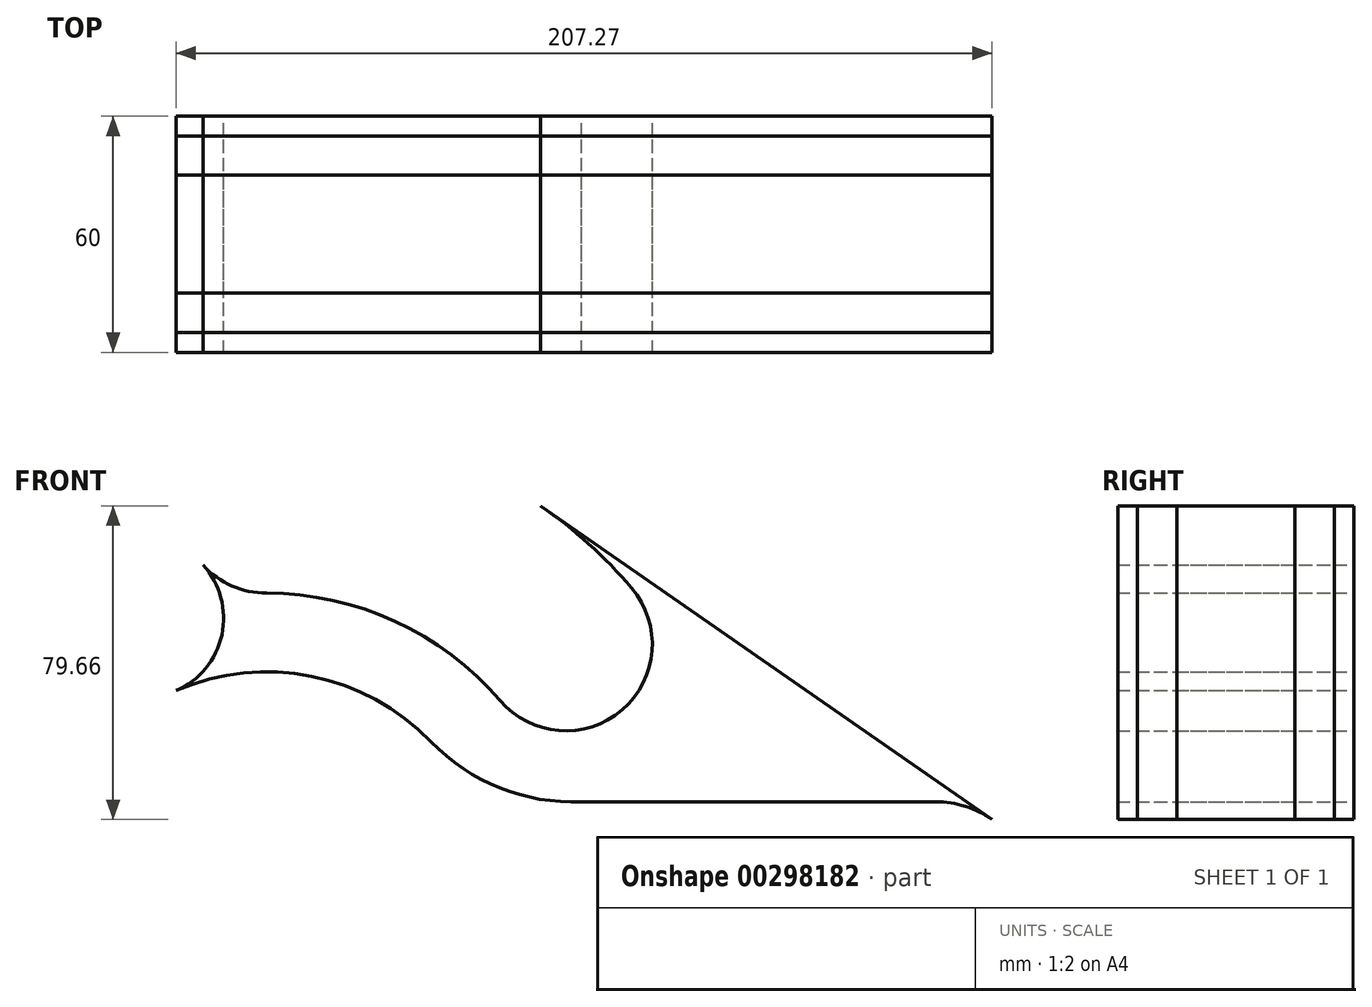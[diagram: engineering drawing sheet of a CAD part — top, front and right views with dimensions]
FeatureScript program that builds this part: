
annotation { "Feature Type Name" : "Feature", "Feature Type Description" : "" }
export const myFeature = defineFeature(function(context is Context, id is Id, definition is map)
    precondition{}
    {
        {
            var Q0;
            Q0=qCreatedBy(makeId("Front.planeOp"),FACE);
            var sketch = newSketch(context, id + "F0", { "sketchPlane" : qUnion([Q0])});
            skLineSegment(sketch, "E0", {"start": v(80, 0) * mm, "end": v(170, 0) * mm, "construction": true});
            skArc(sketch, "E1", {"start": v(0, 100) * mm, "mid": v(41.81, 90.84) * mm, "end": v(75.96, 65.04) * mm, "construction": true});
            skArc(sketch, "E2.0.endCap", {"start": v(170, 25) * mm, "mid": v(195, 0) * mm, "end": v(170, -25) * mm});
            skLineSegment(sketch, "E2.0.left", {"start": v(80, 25) * mm, "end": v(170, 25) * mm});
            skLineSegment(sketch, "E2.0.right", {"start": v(80, -25) * mm, "end": v(170, -25) * mm});
            skArc(sketch, "E3.0.startCap", {"start": v(0, 78) * mm, "mid": v(-22, 100) * mm, "end": v(0, 122) * mm});
            skArc(sketch, "E3.0.endCap", {"start": v(92.68, 79.34) * mm, "mid": v(90.27, 48.32) * mm, "end": v(59.25, 50.73) * mm});
            skArc(sketch, "E3.0.left", {"start": v(0, 122) * mm, "mid": v(51.01, 110.82) * mm, "end": v(92.68, 79.34) * mm});
            skArc(sketch, "E3.0.right", {"start": v(0, 78) * mm, "mid": v(32.61, 70.85) * mm, "end": v(59.25, 50.73) * mm});
            skArc(sketch, "E4.0", {"start": v(0, 91) * mm, "mid": v(38.05, 82.66) * mm, "end": v(69.13, 59.18) * mm});
            skArc(sketch, "E4.1", {"start": v(0, 91) * mm, "mid": v(-9, 100) * mm, "end": v(0, 109) * mm});
            skArc(sketch, "E4.2", {"start": v(0, 109) * mm, "mid": v(45.58, 99.01) * mm, "end": v(82.8, 70.89) * mm});
            skArc(sketch, "E4.3", {"start": v(82.8, 70.89) * mm, "mid": v(81.82, 58.2) * mm, "end": v(69.13, 59.18) * mm});
            skLineSegment(sketch, "E5.0", {"start": v(80, -12.5) * mm, "end": v(170, -12.5) * mm});
            skArc(sketch, "E5.1", {"start": v(80, -12.5) * mm, "mid": v(67.5, 0) * mm, "end": v(80, 12.5) * mm});
            skLineSegment(sketch, "E5.2", {"start": v(80, 12.5) * mm, "end": v(170, 12.5) * mm});
            skArc(sketch, "E5.3", {"start": v(170, 12.5) * mm, "mid": v(182.5, 0) * mm, "end": v(170, -12.5) * mm});
            skCircle(sketch, "E6", {"center": v(0, 0) * mm, "radius": 40 * mm});
            skArc(sketch, "E7", {"start": v(41.76, 40.25) * mm, "mid": v(-58, 0) * mm, "end": v(41.76, -40.25) * mm});
            skArc(sketch, "E8", {"start": v(41.76, 40.25) * mm, "mid": v(59.24, 28.5) * mm, "end": v(80, 25) * mm});
            skArc(sketch, "E9", {"start": v(41.76, -40.25) * mm, "mid": v(59.24, -28.5) * mm, "end": v(80, -25) * mm});
            skLineSegment(sketch, "E10", {"start": v(69.61, 100.2) * mm, "end": v(184.26, 20.53) * mm});
            skArc(sketch, "E11", {"start": v(-23, 53.24) * mm, "mid": v(-11.38, 67.43) * mm, "end": v(-16.2, 85.12) * mm});
            skSolve(sketch);
        }
        {
            var Q0;
            Q0=makeQuery(id+"F0.imprint","IMPRINT",FACE,{"disambiguationData":[TD([[makeQuery(id+"F0.imprint","IMPRINT",EDGE,{"derivedFrom":sQuery(id+"F0.wireOp",EDGE,"E2.0.endCap")}),-1.0]])]});
            extrude(context, id + "F1", {"entities" : qUnion([Q0]), "endBound" : BoundingType.SYMMETRIC, "depth" : 60 * mm});
        }
        {
            var Q0;
            Q0=makeQuery(id+"F0.imprint","IMPRINT",FACE,{"disambiguationData":[TD([[makeQuery(id+"F0.imprint","IMPRINT",EDGE,{"derivedFrom":sQuery(id+"F0.wireOp",EDGE,"E3.0.startCap")}),-1.0]])]});
            extrude(context, id + "F2", {"entities" : qUnion([Q0]), "endBound" : BoundingType.SYMMETRIC, "depth" : 50 * mm});
        }
        {
            var Q0;
            {var subQ4=sQuery(id+"F0.wireOp",EDGE,"E2.0.left");Q0=makeQuery(id+"F0.imprint","IMPRINT",FACE,{"disambiguationData":[TD([[makeQuery(id+"F0.imprint","IMPRINT",EDGE,{"derivedFrom":subQ4}),1.0]])]});}
            extrude(context, id + "F3", {"entities" : qUnion([Q0]), "endBound" : BoundingType.SYMMETRIC, "depth" : 30 * mm});
        }
    });
